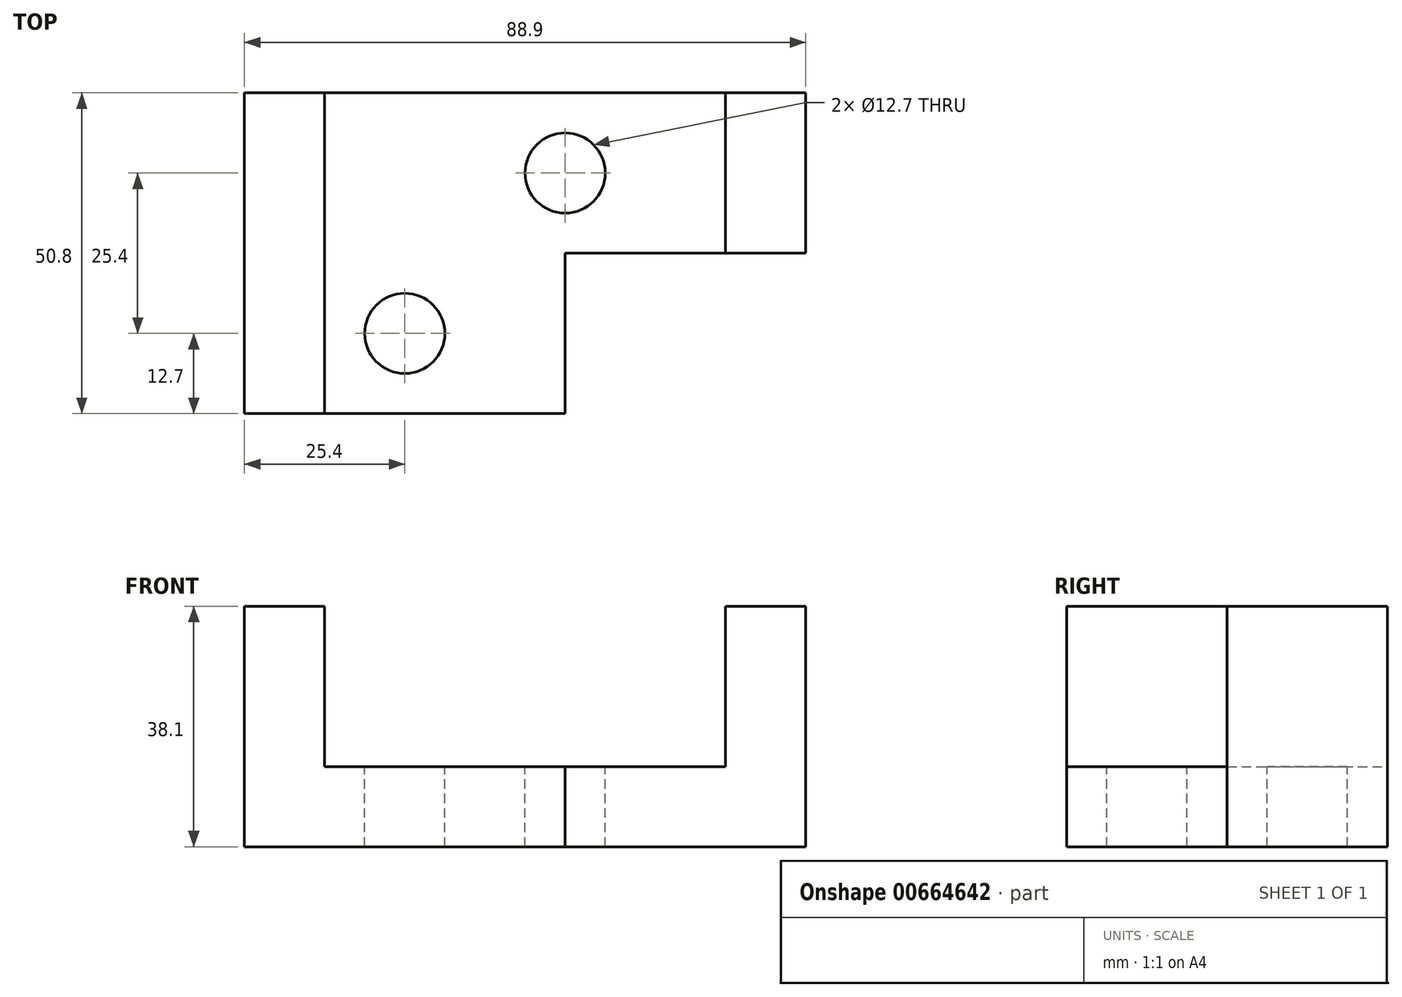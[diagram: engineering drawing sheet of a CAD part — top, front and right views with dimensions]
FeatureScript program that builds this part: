
annotation { "Feature Type Name" : "Feature", "Feature Type Description" : "" }
export const myFeature = defineFeature(function(context is Context, id is Id, definition is map)
    precondition{}
    {
        {
            var Q0;
            Q0=qCreatedBy(makeId("Front.planeOp"),FACE);
            var sketch = newSketch(context, id + "F0", { "sketchPlane" : qUnion([Q0])});
            skLineSegment(sketch, "E0.bottom", {"start": v(-44.45, 17.48) * mm, "end": v(44.45, 17.48) * mm});
            skLineSegment(sketch, "E0.top", {"start": v(-44.45, -20.62) * mm, "end": v(44.45, -20.62) * mm});
            skLineSegment(sketch, "E0.left", {"start": v(-44.45, 17.48) * mm, "end": v(-44.45, -20.62) * mm});
            skLineSegment(sketch, "E0.right", {"start": v(44.45, 17.48) * mm, "end": v(44.45, -20.62) * mm});
            skPoint(sketch, "E0.middle", {"position": v(0, -1.57) * mm});
            skSolve(sketch);
        }
        {
            var Q0;
            Q0=makeQuery(id+"F0.imprint","IMPRINT",FACE,{"disambiguationData":[TD([[makeQuery(id+"F0.imprint","IMPRINT",EDGE,{"derivedFrom":sQuery(id+"F0.wireOp",EDGE,"E0.bottom")}),-1.0]])]});
            extrude(context, id + "F1", {"entities" : qUnion([Q0]), "depth" : 50.8 * mm, "offsetDistance" : 25.4 * mm});
        }
        {
            var Q0;
            Q0=qCreatedBy(makeId("Front.planeOp"),FACE);
            var sketch = newSketch(context, id + "F2", { "sketchPlane" : qUnion([Q0])});
            skLineSegment(sketch, "E1.bottom", {"start": v(-31.75, 17.48) * mm, "end": v(31.75, 17.48) * mm});
            skLineSegment(sketch, "E1.top", {"start": v(-31.75, -7.92) * mm, "end": v(31.75, -7.92) * mm});
            skLineSegment(sketch, "E1.left", {"start": v(-31.75, 17.48) * mm, "end": v(-31.75, -7.92) * mm});
            skLineSegment(sketch, "E1.right", {"start": v(31.75, 17.48) * mm, "end": v(31.75, -7.92) * mm});
            skSolve(sketch);
        }
        {
            var Q0;
            Q0=makeQuery(id+"F2.imprint","IMPRINT",FACE,{"disambiguationData":[TD([[makeQuery(id+"F2.imprint","IMPRINT",EDGE,{"derivedFrom":sQuery(id+"F2.wireOp",EDGE,"E1.bottom")}),-1.0]])]});
            extrude(context, id + "F3", {"entities" : qUnion([Q0]), "operationType" : NewBodyOperationType.REMOVE, "endBound" : BoundingType.THROUGH_ALL, "depth" : 25.4 * mm, "offsetDistance" : 25.4 * mm});
        }
        {
            var Q0;
            Q0=qCreatedBy(makeId("Top.planeOp"),FACE);
            var sketch = newSketch(context, id + "F4", { "sketchPlane" : qUnion([Q0])});
            skLineSegment(sketch, "E2.bottom", {"start": v(44.45, -50.8) * mm, "end": v(6.35, -50.8) * mm});
            skLineSegment(sketch, "E2.top", {"start": v(44.45, -25.4) * mm, "end": v(6.35, -25.4) * mm});
            skLineSegment(sketch, "E2.left", {"start": v(44.45, -50.8) * mm, "end": v(44.45, -25.4) * mm});
            skLineSegment(sketch, "E2.right", {"start": v(6.35, -50.8) * mm, "end": v(6.35, -25.4) * mm});
            skSolve(sketch);
        }
        {
            var Q0;
            Q0=makeQuery(id+"F4.imprint","IMPRINT",FACE,{"disambiguationData":[TD([[makeQuery(id+"F4.imprint","IMPRINT",EDGE,{"derivedFrom":sQuery(id+"F4.wireOp",EDGE,"E2.bottom")}),-1.0]])]});
            extrude(context, id + "F5", {"entities" : qUnion([Q0]), "operationType" : NewBodyOperationType.REMOVE, "endBound" : BoundingType.THROUGH_ALL, "oppositeDirection" : true, "depth" : 25.4 * mm, "offsetDistance" : 25.4 * mm});
        }
        {
            var Q0;
            Q0=qCreatedBy(makeId("Top.planeOp"),FACE);
            var sketch = newSketch(context, id + "F6", { "sketchPlane" : qUnion([Q0])});
            skLineSegment(sketch, "E3.bottom", {"start": v(31.7, -25.4) * mm, "end": v(44.4, -25.4) * mm});
            skLineSegment(sketch, "E3.top", {"start": v(31.7, -50.8) * mm, "end": v(44.4, -50.8) * mm});
            skLineSegment(sketch, "E3.left", {"start": v(31.7, -25.4) * mm, "end": v(31.7, -50.8) * mm});
            skLineSegment(sketch, "E3.right", {"start": v(44.4, -25.4) * mm, "end": v(44.4, -50.8) * mm});
            skSolve(sketch);
        }
        {
            var Q0;
            {var subQ0=sQuery(id+"F0.wireOp",EDGE,"E0.right");var subQ3=sQuery(id+"F0.wireOp",EDGE,"E0.bottom");Q0=makeQuery(id+"F3.boolean.opBoolean","SPLIT",FACE,{"disambiguationData":[TD([makeQuery(id+"F1.opExtrude","SWEPT_FACE",FACE,{"disambiguationData":[OSD([subQ0])]})])],"derivedFrom":makeQuery(id+"F1.opExtrude","SWEPT_FACE",FACE,{"disambiguationData":[OSD([subQ3])]})});}
            var Q1;
            Q1=makeQuery(id+"F6.imprint","IMPRINT",FACE,{"disambiguationData":[TD([[makeQuery(id+"F6.imprint","IMPRINT",EDGE,{"derivedFrom":sQuery(id+"F6.wireOp",EDGE,"E3.bottom")}),-1.0]])]});
            extrude(context, id + "F7", {"entities" : qUnion([Q0, Q1]), "operationType" : NewBodyOperationType.REMOVE, "depth" : 25.4 * mm, "offsetDistance" : 25.4 * mm});
        }
        {
            var Q0;
            Q0=makeQuery(id+"F7.boolean.opBoolean","COPY",FACE,{"derivedFrom":makeQuery(id+"F7.opExtrude","SWEPT_FACE",FACE,{"disambiguationData":[OSD([sQuery(id+"F6.wireOp",EDGE,"E3.right")])]})});
            extrude(context, id + "F8", {"entities" : qUnion([Q0]), "operationType" : NewBodyOperationType.REMOVE, "endBound" : BoundingType.THROUGH_ALL, "oppositeDirection" : true, "depth" : 25.4 * mm, "offsetDistance" : 25.4 * mm});
        }
        {
            var Q0;
            Q0=qCreatedBy(makeId("Top.planeOp"),FACE);
            var sketch = newSketch(context, id + "F9", { "sketchPlane" : qUnion([Q0])});
            skCircle(sketch, "E4", {"center": v(-19.05, -38.1) * mm, "radius": 6.35 * mm});
            skCircle(sketch, "E5", {"center": v(6.35, -12.7) * mm, "radius": 6.35 * mm});
            skSolve(sketch);
        }
        {
            var Q0;
            Q0=makeQuery(id+"F9.imprint","IMPRINT",FACE,{"disambiguationData":[TD([[makeQuery(id+"F9.imprint","IMPRINT",EDGE,{"derivedFrom":sQuery(id+"F9.wireOp",EDGE,"E4")}),1.0]])]});
            extrude(context, id + "F10", {"entities" : qUnion([Q0]), "operationType" : NewBodyOperationType.REMOVE, "endBound" : BoundingType.THROUGH_ALL, "oppositeDirection" : true, "depth" : 25.4 * mm, "offsetDistance" : 25.4 * mm});
        }
        {
            var Q0;
            Q0=qCreatedBy(makeId("Top.planeOp"),FACE);
            var sketch = newSketch(context, id + "F11", { "sketchPlane" : qUnion([Q0])});
            skCircle(sketch, "E6", {"center": v(6.35, -12.7) * mm, "radius": 6.35 * mm});
            skSolve(sketch);
        }
        {
            var Q0;
            Q0=makeQuery(id+"F11.imprint","IMPRINT",FACE,{"disambiguationData":[TD([[makeQuery(id+"F11.imprint","IMPRINT",EDGE,{"derivedFrom":sQuery(id+"F11.wireOp",EDGE,"E6")}),1.0]])]});
            extrude(context, id + "F12", {"entities" : qUnion([Q0]), "operationType" : NewBodyOperationType.REMOVE, "endBound" : BoundingType.THROUGH_ALL, "oppositeDirection" : true, "depth" : 25.4 * mm, "offsetDistance" : 25.4 * mm});
        }
    });
